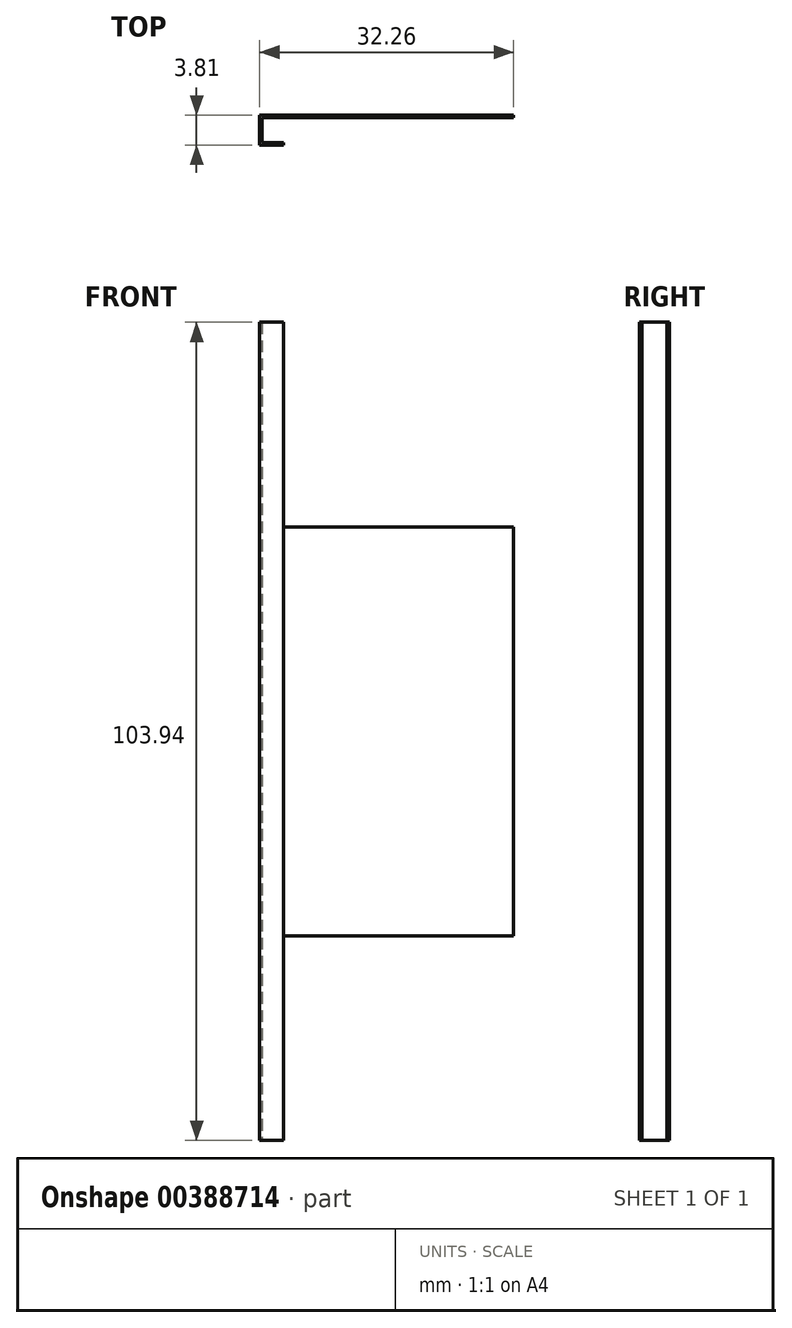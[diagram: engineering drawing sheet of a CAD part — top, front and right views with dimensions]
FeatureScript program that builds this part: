
annotation { "Feature Type Name" : "Feature", "Feature Type Description" : "" }
export const myFeature = defineFeature(function(context is Context, id is Id, definition is map)
    precondition{}
    {
        {
            var Q0;
            Q0=qCreatedBy(makeId("Front.planeOp"),FACE);
            var sketch = newSketch(context, id + "F0", { "sketchPlane" : qUnion([Q0])});
            skLineSegment(sketch, "E0.bottom", {"start": v(-1.52, -51.97) * mm, "end": v(1.52, -51.97) * mm});
            skLineSegment(sketch, "E0.top", {"start": v(-1.52, 51.97) * mm, "end": v(1.52, 51.97) * mm});
            skLineSegment(sketch, "E0.left", {"start": v(-1.52, -51.97) * mm, "end": v(-1.52, 51.97) * mm});
            skLineSegment(sketch, "E0.right", {"start": v(1.52, -51.97) * mm, "end": v(1.52, 51.97) * mm});
            skSolve(sketch);
        }
        {
            var Q0;
            Q0 = qSketchRegion(id + "F0", true);
            extrude(context, id + "F1", {"entities" : qUnion([Q0]), "depth" : 3.8 * mm});
        }
        {
            var Q0;
            Q0=makeQuery(id+"F1.opExtrude","SWEPT_FACE",FACE,{"disambiguationData":[OSD([sQuery(id+"F0.wireOp",EDGE,"E0.right")])]});
            var sketch = newSketch(context, id + "F2", { "sketchPlane" : qUnion([Q0])});
            skLineSegment(sketch, "E1.bottom", {"start": v(-3.5, 51.97) * mm, "end": v(-0.32, 51.97) * mm});
            skLineSegment(sketch, "E1.top", {"start": v(-3.5, -51.97) * mm, "end": v(-0.32, -51.97) * mm});
            skLineSegment(sketch, "E1.left", {"start": v(-3.5, 51.97) * mm, "end": v(-3.5, -51.97) * mm});
            skLineSegment(sketch, "E1.right", {"start": v(-0.32, 51.97) * mm, "end": v(-0.32, -51.97) * mm});
            skSolve(sketch);
        }
        {
            var Q0;
            Q0 = qSketchRegion(id + "F2", true);
            extrude(context, id + "F3", {"entities" : qUnion([Q0]), "operationType" : NewBodyOperationType.REMOVE, "oppositeDirection" : true, "depth" : 2.72 * mm});
        }
        {
            var Q0;
            {var subQ1=sQuery(id+"F0.wireOp",EDGE,"E0.right");Q0=makeQuery(id+"F3.boolean.opBoolean","SPLIT",FACE,{"disambiguationData":[TD([makeQuery(id+"F3.opExtrude","SWEPT_FACE",FACE,{"disambiguationData":[OSD([sQuery(id+"F2.wireOp",EDGE,"E1.right")])]})])],"derivedFrom":makeQuery(id+"F1.opExtrude","SWEPT_FACE",FACE,{"disambiguationData":[OSD([subQ1])]})});}
            var sketch = newSketch(context, id + "F4", { "sketchPlane" : qUnion([Q0])});
            skLineSegment(sketch, "E2.bottom", {"start": v(-0.32, 25.98) * mm, "end": v(0, 25.98) * mm});
            skLineSegment(sketch, "E2.top", {"start": v(-0.32, -25.98) * mm, "end": v(0, -25.98) * mm});
            skLineSegment(sketch, "E2.left", {"start": v(-0.32, 25.98) * mm, "end": v(-0.32, -25.98) * mm});
            skLineSegment(sketch, "E2.right", {"start": v(0, 25.98) * mm, "end": v(0, -25.98) * mm});
            skSolve(sketch);
        }
        {
            var Q0;
            Q0 = qSketchRegion(id + "F4", true);
            extrude(context, id + "F5", {"entities" : qUnion([Q0]), "operationType" : NewBodyOperationType.ADD, "depth" : 29.22 * mm});
        }
    });
